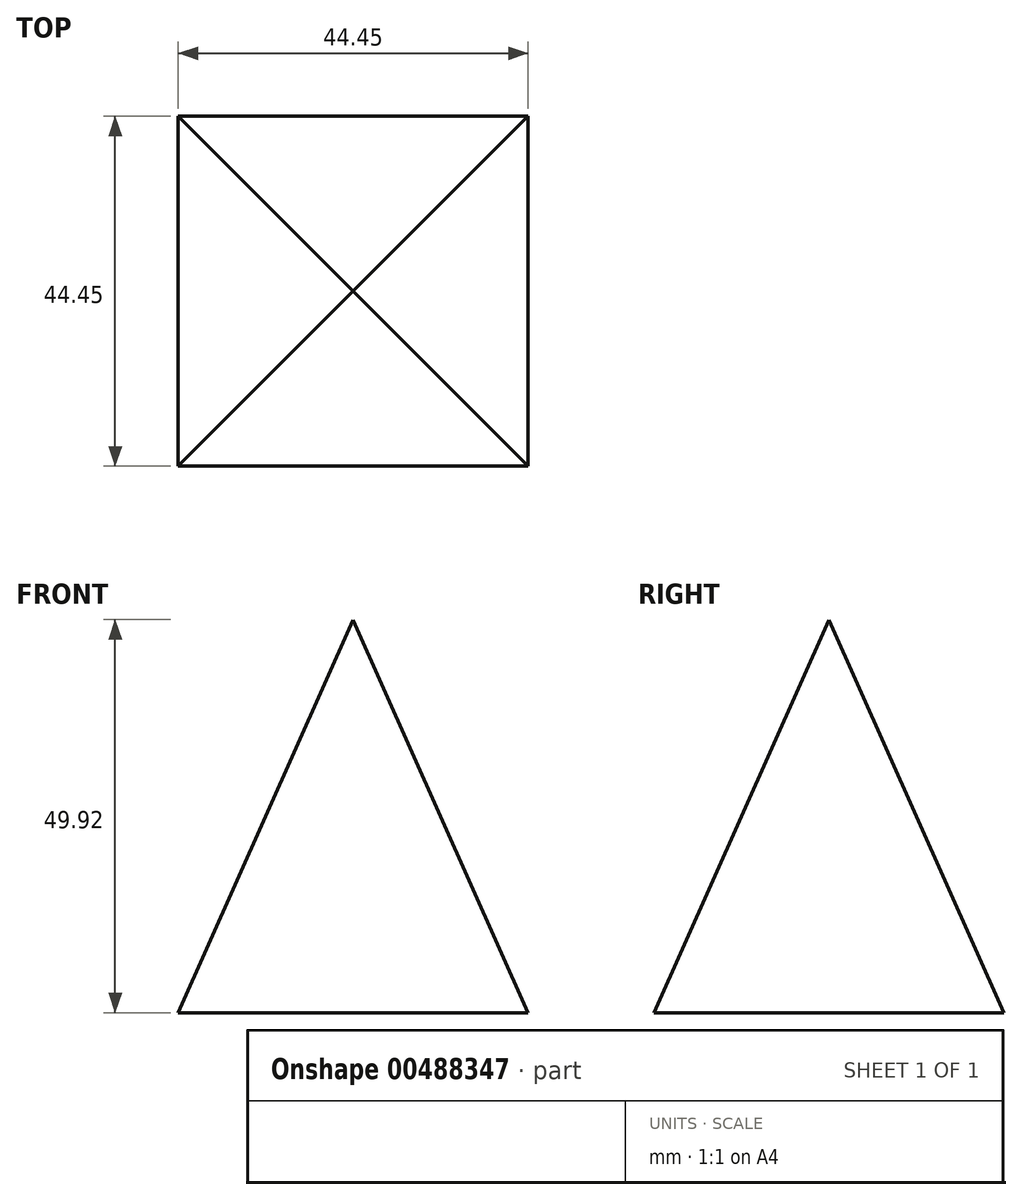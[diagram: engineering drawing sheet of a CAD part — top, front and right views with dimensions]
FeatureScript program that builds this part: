
annotation { "Feature Type Name" : "Feature", "Feature Type Description" : "" }
export const myFeature = defineFeature(function(context is Context, id is Id, definition is map)
    precondition{}
    {
        {
            var Q0;
            Q0=qCreatedBy(makeId("Top.planeOp"),FACE);
            var sketch = newSketch(context, id + "F0", { "sketchPlane" : qUnion([Q0])});
            skLineSegment(sketch, "E0.bottom", {"start": v(-24.5, 27.35) * mm, "end": v(19.94, 27.35) * mm});
            skLineSegment(sketch, "E0.top", {"start": v(-24.5, -17.1) * mm, "end": v(19.94, -17.1) * mm});
            skLineSegment(sketch, "E0.left", {"start": v(-24.5, 27.35) * mm, "end": v(-24.5, -17.1) * mm});
            skLineSegment(sketch, "E0.right", {"start": v(19.94, 27.35) * mm, "end": v(19.94, -17.1) * mm});
            skSolve(sketch);
        }
        {
            var Q0;
            Q0=makeQuery(id+"F0.imprint","IMPRINT",FACE,{"disambiguationData":[TD([[makeQuery(id+"F0.imprint","IMPRINT",EDGE,{"derivedFrom":sQuery(id+"F0.wireOp",EDGE,"E0.bottom")}),-1.0]])]});
            extrude(context, id + "F1", {"entities" : qUnion([Q0]), "depth" : 50.8 * mm, "hasDraft" : true, "draftAngle" : 24 * degree, "draftPullDirection" : true});
        }
    });
